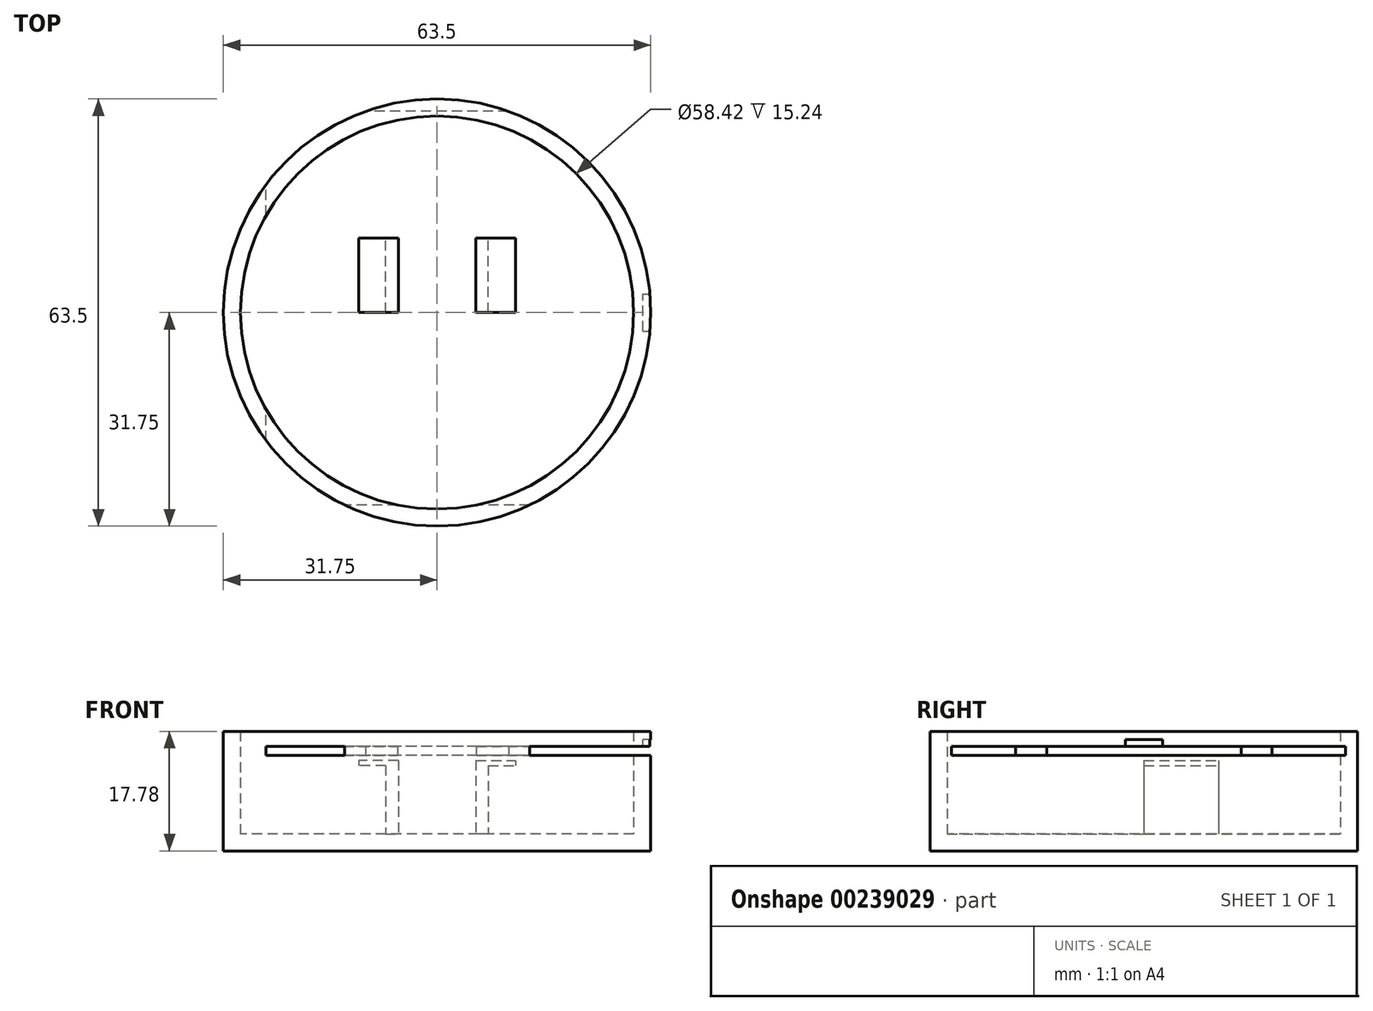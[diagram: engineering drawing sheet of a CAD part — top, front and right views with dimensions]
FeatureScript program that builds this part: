
annotation { "Feature Type Name" : "Feature", "Feature Type Description" : "" }
export const myFeature = defineFeature(function(context is Context, id is Id, definition is map)
    precondition{}
    {
        {
            var Q0;
            Q0=qCreatedBy(makeId("Top.planeOp"),FACE);
            var sketch = newSketch(context, id + "F0", { "sketchPlane" : qUnion([Q0])});
            skCircle(sketch, "E0", {"center": v(0, 0) * mm, "radius": 31.75 * mm});
            skSolve(sketch);
        }
        {
            var Q0;
            Q0 = qSketchRegion(id + "F0", true);
            extrude(context, id + "F1", {"entities" : qUnion([Q0]), "depth" : 17.78 * mm});
        }
        {
            var Q0;
            Q0=makeQuery(id+"F1.opExtrude","CAP_FACE",FACE,{"disambiguationData":[OSD([sQuery(id+"F0.wireOp",EDGE,"E0")])],"isStart":false});
            shell(context, id + "F2", {"entities" : qUnion([Q0]), "thickness" : 2.54 * mm});
        }
        {
            var Q0;
            {var subQ0=sQuery(id+"F0.wireOp",EDGE,"E0");Q0=makeQuery(id+"F2.opShell","OFFSET_FACE",FACE,{"disambiguationData":[OSD([subQ0]),TDD([makeQuery(id+"F1.opExtrude","CAP_FACE",FACE,{"disambiguationData":[OSD([subQ0])],"isStart":true})])]});}
            var sketch = newSketch(context, id + "F3", { "sketchPlane" : qUnion([Q0])});
            skLineSegment(sketch, "E1.bottom", {"start": v(-7.62, 0) * mm, "end": v(-5.76, 0) * mm});
            skLineSegment(sketch, "E1.top", {"start": v(-7.62, 11.06) * mm, "end": v(-5.76, 11.06) * mm});
            skLineSegment(sketch, "E1.left", {"start": v(-7.62, 0) * mm, "end": v(-7.62, 11.06) * mm});
            skLineSegment(sketch, "E1.right", {"start": v(-5.76, 0) * mm, "end": v(-5.76, 11.06) * mm});
            skLineSegment(sketch, "E2.MirrorCS", {"start": v(5.76, 0) * mm, "end": v(5.76, 11.06) * mm});
            skLineSegment(sketch, "E3.MirrorCS", {"start": v(7.62, 0) * mm, "end": v(7.62, 11.06) * mm});
            skLineSegment(sketch, "E4.MirrorCS", {"start": v(7.62, 11.06) * mm, "end": v(5.76, 11.06) * mm});
            skLineSegment(sketch, "E5.MirrorCS", {"start": v(7.62, 0) * mm, "end": v(5.76, 0) * mm});
            skSolve(sketch);
        }
        {
            var Q0;
            Q0 = qSketchRegion(id + "F3", true);
            extrude(context, id + "F4", {"entities" : qUnion([Q0]), "operationType" : NewBodyOperationType.ADD, "depth" : 10.16 * mm});
        }
        {
            var Q0;
            Q0=makeQuery(id+"F4.opExtrude","CAP_FACE",FACE,{"disambiguationData":[OSD([sQuery(id+"F3.wireOp",EDGE,"E1.bottom"),sQuery(id+"F3.wireOp",EDGE,"E1.top"),sQuery(id+"F3.wireOp",EDGE,"E1.left"),sQuery(id+"F3.wireOp",EDGE,"E1.right")])],"isStart":false});
            var sketch = newSketch(context, id + "F5", { "sketchPlane" : qUnion([Q0])});
            skLineSegment(sketch, "E6.bottom", {"start": v(-5.76, 11.06) * mm, "end": v(-11.67, 11.06) * mm});
            skLineSegment(sketch, "E6.top", {"start": v(-5.76, 0) * mm, "end": v(-11.67, 0) * mm});
            skLineSegment(sketch, "E6.left", {"start": v(-5.76, 11.06) * mm, "end": v(-5.76, 0) * mm});
            skLineSegment(sketch, "E6.right", {"start": v(-11.67, 11.06) * mm, "end": v(-11.67, 0) * mm});
            skLineSegment(sketch, "E7.MirrorCS", {"start": v(5.76, 11.06) * mm, "end": v(5.76, 0) * mm});
            skLineSegment(sketch, "E8.MirrorCS", {"start": v(5.76, 11.06) * mm, "end": v(11.67, 11.06) * mm});
            skLineSegment(sketch, "E9.MirrorCS", {"start": v(11.67, 11.06) * mm, "end": v(11.67, 0) * mm});
            skLineSegment(sketch, "E10.MirrorCS", {"start": v(5.76, 0) * mm, "end": v(11.67, 0) * mm});
            skSolve(sketch);
        }
        {
            var Q0;
            Q0 = qSketchRegion(id + "F5", true);
            extrude(context, id + "F6", {"entities" : qUnion([Q0]), "operationType" : NewBodyOperationType.ADD, "depth" : 0.76 * mm});
        }
        {
            var Q0;
            Q0=qCreatedBy(makeId("Right.planeOp"),FACE);
            var sketch = newSketch(context, id + "F7", { "sketchPlane" : qUnion([Q0])});
            skLineSegment(sketch, "E11.bottom", {"start": v(-28.62, 15.52) * mm, "end": v(29.92, 15.52) * mm});
            skLineSegment(sketch, "E11.top", {"start": v(-28.62, 14.22) * mm, "end": v(29.92, 14.22) * mm});
            skLineSegment(sketch, "E11.left", {"start": v(-28.62, 15.52) * mm, "end": v(-28.62, 14.22) * mm});
            skLineSegment(sketch, "E11.right", {"start": v(29.92, 15.52) * mm, "end": v(29.92, 14.22) * mm});
            skSolve(sketch);
        }
        {
            var Q0;
            Q0 = qSketchRegion(id + "F7", true);
            extrude(context, id + "F8", {"entities" : qUnion([Q0]), "operationType" : NewBodyOperationType.REMOVE, "depth" : 43.43 * mm, "hasSecondDirection" : true, "secondDirectionOppositeDirection" : true, "secondDirectionDepth" : 25.4 * mm});
        }
        {
            var Q0;
            Q0=qCreatedBy(makeId("Right.planeOp"),FACE);
            var sketch = newSketch(context, id + "F9", { "sketchPlane" : qUnion([Q0])});
            skLineSegment(sketch, "E12.bottom", {"start": v(-2.78, 15.14) * mm, "end": v(0, 15.14) * mm});
            skLineSegment(sketch, "E12.top", {"start": v(-2.78, 16.55) * mm, "end": v(0, 16.55) * mm});
            skLineSegment(sketch, "E12.left", {"start": v(-2.78, 15.14) * mm, "end": v(-2.78, 16.55) * mm});
            skLineSegment(sketch, "E12.right", {"start": v(0, 15.14) * mm, "end": v(0, 16.55) * mm});
            skLineSegment(sketch, "E13.MirrorCS", {"start": v(2.78, 15.14) * mm, "end": v(0, 15.14) * mm});
            skLineSegment(sketch, "E14.MirrorCS", {"start": v(2.78, 16.55) * mm, "end": v(0, 16.55) * mm});
            skLineSegment(sketch, "E15.MirrorCS", {"start": v(2.78, 15.14) * mm, "end": v(2.78, 16.55) * mm});
            skSolve(sketch);
        }
        {
            var Q0;
            Q0 = qSketchRegion(id + "F9", true);
            extrude(context, id + "F10", {"entities" : qUnion([Q0]), "operationType" : NewBodyOperationType.REMOVE, "depth" : 34.3 * mm, "hasSecondDirection" : true, "secondDirectionOppositeDirection" : false, "secondDirectionDepth" : 30.6 * mm});
        }
    });
